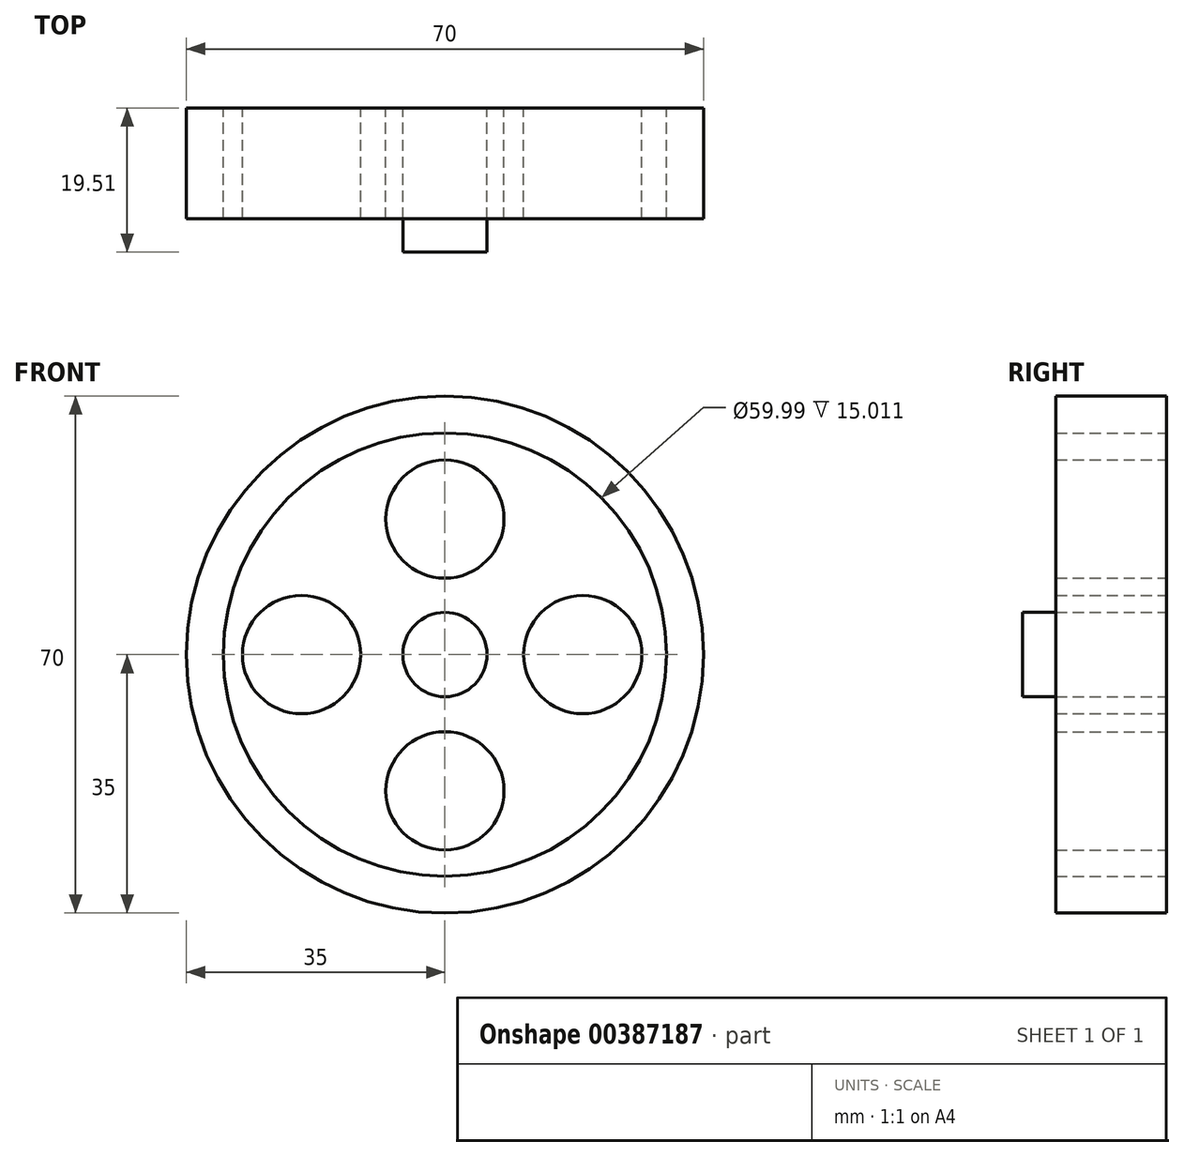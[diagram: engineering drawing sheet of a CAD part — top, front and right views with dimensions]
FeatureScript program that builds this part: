
annotation { "Feature Type Name" : "Feature", "Feature Type Description" : "" }
export const myFeature = defineFeature(function(context is Context, id is Id, definition is map)
    precondition{}
    {
        {
            var Q0;
            Q0=qCreatedBy(makeId("Front.planeOp"),FACE);
            var sketch = newSketch(context, id + "F0", { "sketchPlane" : qUnion([Q0])});
            skPoint(sketch, "E0.middle", {"position": v(0, 0) * mm});
            skCircle(sketch, "E1", {"center": v(0, 0) * mm, "radius": 35 * mm});
            skCircle(sketch, "E2", {"center": v(0, 0) * mm, "radius": 30 * mm});
            skCircle(sketch, "E3", {"center": v(0, 0) * mm, "radius": 10 * mm});
            skCircle(sketch, "E4", {"center": v(0, 0) * mm, "radius": 5.7 * mm});
            skCircle(sketch, "E5", {"center": v(0, 18.35) * mm, "radius": 8 * mm});
            skCircle(sketch, "E6", {"center": v(18.67, 0) * mm, "radius": 8 * mm});
            skCircle(sketch, "E7", {"center": v(0, -18.45) * mm, "radius": 8 * mm});
            skCircle(sketch, "E8", {"center": v(-19.4, 0) * mm, "radius": 8 * mm});
            skSolve(sketch);
        }
        {
            var Q0;
            Q0=makeQuery(id+"F0.imprint","IMPRINT",FACE,{"disambiguationData":[TD([[makeQuery(id+"F0.imprint","IMPRINT",EDGE,{"derivedFrom":sQuery(id+"F0.wireOp",EDGE,"E4")}),1.0]])]});
            extrude(context, id + "F1", {"entities" : qUnion([Q0]), "depth" : 19.5 * mm});
        }
        {
            var Q0;
            Q0=makeQuery(id+"F0.imprint","IMPRINT",FACE,{"disambiguationData":[TD([[makeQuery(id+"F0.imprint","IMPRINT",EDGE,{"derivedFrom":sQuery(id+"F0.wireOp",EDGE,"E1")}),1.0]])]});
            var Q1;
            Q1=makeQuery(id+"F0.imprint","IMPRINT",FACE,{"disambiguationData":[TD([[makeQuery(id+"F0.imprint","IMPRINT",EDGE,{"derivedFrom":sQuery(id+"F0.wireOp",EDGE,"E8")}),1.0]])]});
            var Q2;
            Q2=makeQuery(id+"F0.imprint","IMPRINT",FACE,{"disambiguationData":[TD([[makeQuery(id+"F0.imprint","IMPRINT",EDGE,{"derivedFrom":sQuery(id+"F0.wireOp",EDGE,"E5")}),1.0]])]});
            var Q3;
            Q3=makeQuery(id+"F0.imprint","IMPRINT",FACE,{"disambiguationData":[TD([[makeQuery(id+"F0.imprint","IMPRINT",EDGE,{"derivedFrom":sQuery(id+"F0.wireOp",EDGE,"E6")}),1.0]])]});
            var Q4;
            Q4=makeQuery(id+"F0.imprint","IMPRINT",FACE,{"disambiguationData":[TD([[makeQuery(id+"F0.imprint","IMPRINT",EDGE,{"derivedFrom":sQuery(id+"F0.wireOp",EDGE,"E7")}),1.0]])]});
            extrude(context, id + "F2", {"entities" : qUnion([Q0, Q1, Q2, Q3, Q4]), "depth" : 15 * mm});
        }
    });
